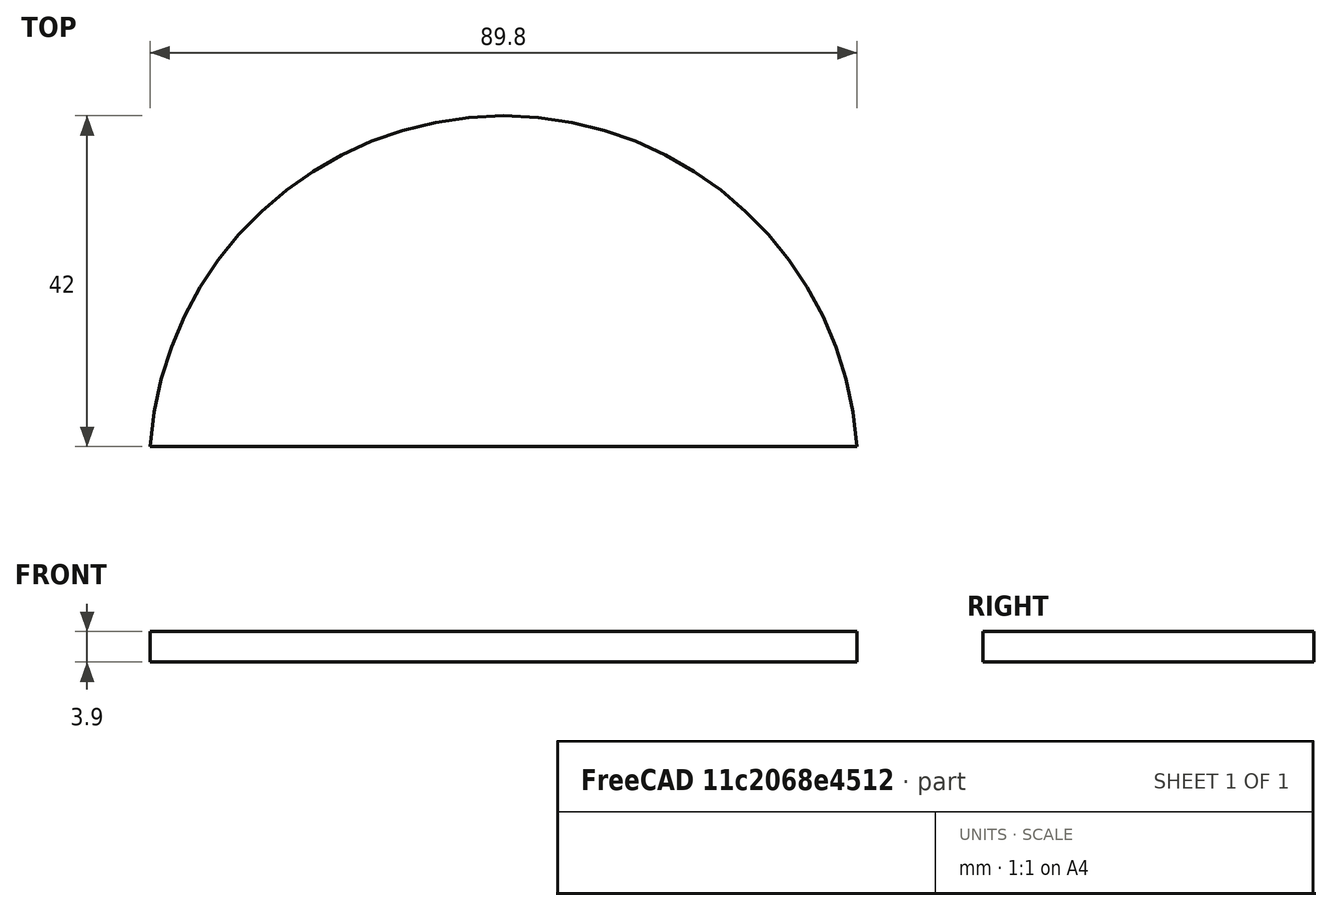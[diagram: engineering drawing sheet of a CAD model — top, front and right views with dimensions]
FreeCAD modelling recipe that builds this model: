
FCSTD DOCUMENT  (FreeCAD 1.0R39319 (Git))
Label: cylinder_90x6_with_2cuts
License: All rights reserved
LicenseURL: https://en.wikipedia.org/wiki/All_rights_reserved
objects: Sketcher::SketchObject×3, PartDesign::Pocket×2, PartDesign::Pad×1, PartDesign::Body×1
note: 16 computed .brp shape members not serialized (recipe doc carries the construction recipe); baked Part::Feature solids carry a one-line shape summary decoded from their .brp

FEATURE [Sketcher::SketchObject] Sketch_1
  ArcFitTolerance = 1e-06
  AttachmentSupport = -> [XY_Plane]
  FullyConstrained = false
  MakeInternals = false
  MapMode = 5
  sketch-geometry (1):
    g0: Circle CenterX=0 CenterY=0 CenterZ=0 NormalX=0 NormalY=0 NormalZ=1 AngleXU=0 Radius=45
FEATURE [PartDesign::Pad] Pad_1
  Direction = (0,0,1)
  Length = 6.9
  Length2 = 10
  Profile = -> Sketch_1
  Refine = true
  Suppressed = false
  Type = 0
FEATURE [Sketcher::SketchObject] Sketch_2
  ArcFitTolerance = 1e-06
  AttachmentSupport = -> [Pad_1]
  FullyConstrained = false
  MakeInternals = false
  MapMode = 5
  Placement = pos=(0,0,6.9) rot=(0,0,1;0rad)
  sketch-geometry (4):
    g0: LineSegment StartX=-45 StartY=-3 StartZ=0 EndX=45 EndY=-3 EndZ=0
    g1: LineSegment StartX=45 StartY=-3 StartZ=0 EndX=45 EndY=3 EndZ=0
    g2: LineSegment StartX=45 StartY=3 StartZ=0 EndX=-45 EndY=3 EndZ=0
    g3: LineSegment StartX=-45 StartY=3 StartZ=0 EndX=-45 EndY=-3 EndZ=0
  constraints (4):
    c: Coincident(g0,g1)
    c: Coincident(g1,g2)
    c: Coincident(g2,g3)
    c: Coincident(g3,g0)
FEATURE [PartDesign::Pocket] Pocket_2
  BaseFeature = -> Pad_1
  Direction = (0,0,-1)
  Length = 5
  Length2 = 5
  Profile = -> Sketch_2
  Refine = true
  Suppressed = false
  Type = 1
FEATURE [Sketcher::SketchObject] Sketch_3
  ArcFitTolerance = 1e-06
  AttachmentSupport = -> [Pocket_2]
  FullyConstrained = false
  MakeInternals = false
  MapMode = 5
  Placement = pos=(0,3,0) rot=(1,0,0;1.5708rad)
  sketch-geometry (4):
    g0: LineSegment StartX=-45 StartY=-3 StartZ=0 EndX=45 EndY=-3 EndZ=0
    g1: LineSegment StartX=45 StartY=-3 StartZ=0 EndX=45 EndY=3 EndZ=0
    g2: LineSegment StartX=45 StartY=3 StartZ=0 EndX=-45 EndY=3 EndZ=0
    g3: LineSegment StartX=-45 StartY=3 StartZ=0 EndX=-45 EndY=-3 EndZ=0
  constraints (4):
    c: Coincident(g0,g1)
    c: Coincident(g1,g2)
    c: Coincident(g2,g3)
    c: Coincident(g3,g0)
FEATURE [PartDesign::Pocket] Pocket_3
  BaseFeature = -> Pocket_2
  Direction = (0,1,-2e-16)
  Length = 5
  Length2 = 5
  Profile = -> Sketch_3
  Refine = true
  Suppressed = false
  Type = 1
FEATURE [PartDesign::Body] Body
  AllowCompound = false
  Group = -> [Sketch_1,Pad_1,Sketch_2,Pocket_2,Sketch_3,Pocket_3]
  Origin = -> Origin
  Tip = -> Pocket_3
